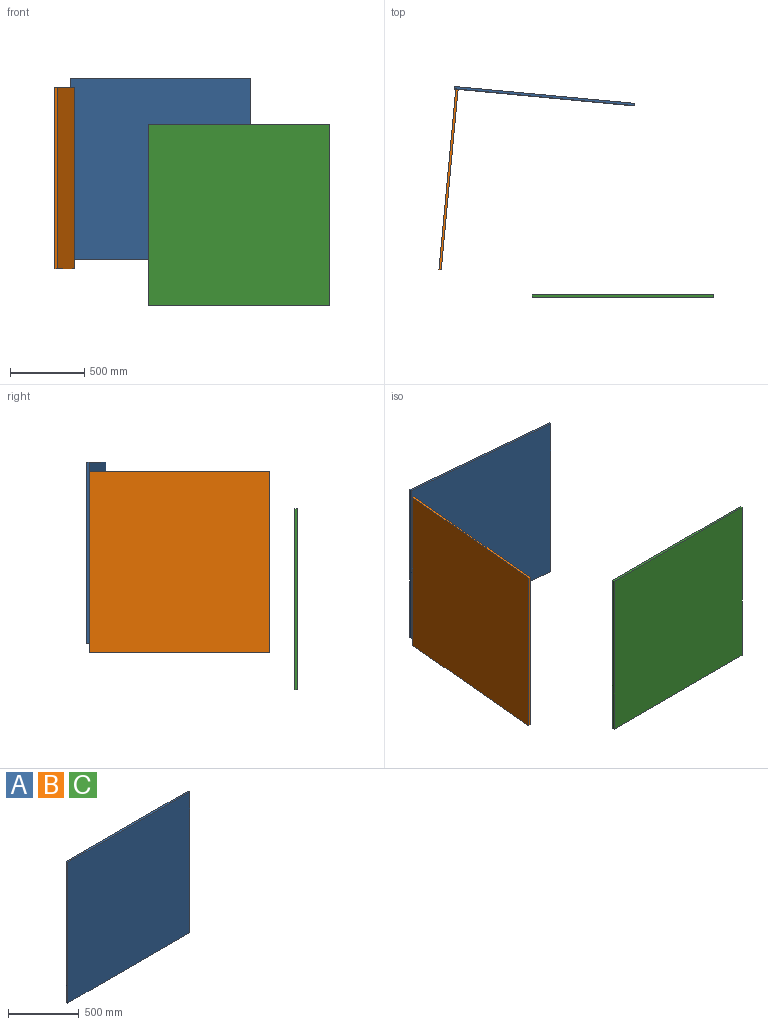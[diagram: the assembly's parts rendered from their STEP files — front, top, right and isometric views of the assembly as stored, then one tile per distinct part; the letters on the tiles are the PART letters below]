
ASSEMBLY  parts=3 mates=1
PART A: 6 faces, bbox 1219.2x15.9x1219.2 mm
  f0: plane 1219.2x15.88mm, normal (1,0,0), area 19354.8mm2, adj f1,f3,f4,f5
  f1: plane 1219.2x15.88mm, normal (0,0,1), area 19354.8mm2, adj f0,f2,f4,f5
  f2: plane 1219.2x15.88mm, normal (-1,0,0), area 19354.8mm2, adj f1,f3,f4,f5
  f3: plane 1219.2x15.88mm, normal (0,0,-1), area 19354.8mm2, adj f0,f2,f4,f5
  f4: plane 1219.2x1219.2mm, normal (0,-1,0), area 1486448.6mm2, adj f0,f1,f2,f3
  f5: plane 1219.2x1219.2mm, normal (0,1,0), area 1486448.6mm2, adj f0,f1,f2,f3
PART B: same geometry as A
PART C: same geometry as A
PLACE A rot(axis=(0,0,-1),5.3deg) t=(-584.54,20.43,289.42)mm
PLACE B rot(axis=(0,0,1),84.7deg) t=(-1237.97,-546.69,225.87)mm
PLACE C t=(-57.72,-1326,-21.12)mm
MATE planar A.f4 <-> B.f0  axis (-0.09,-1,0) through (-586.02,4.63,289.42)mm
